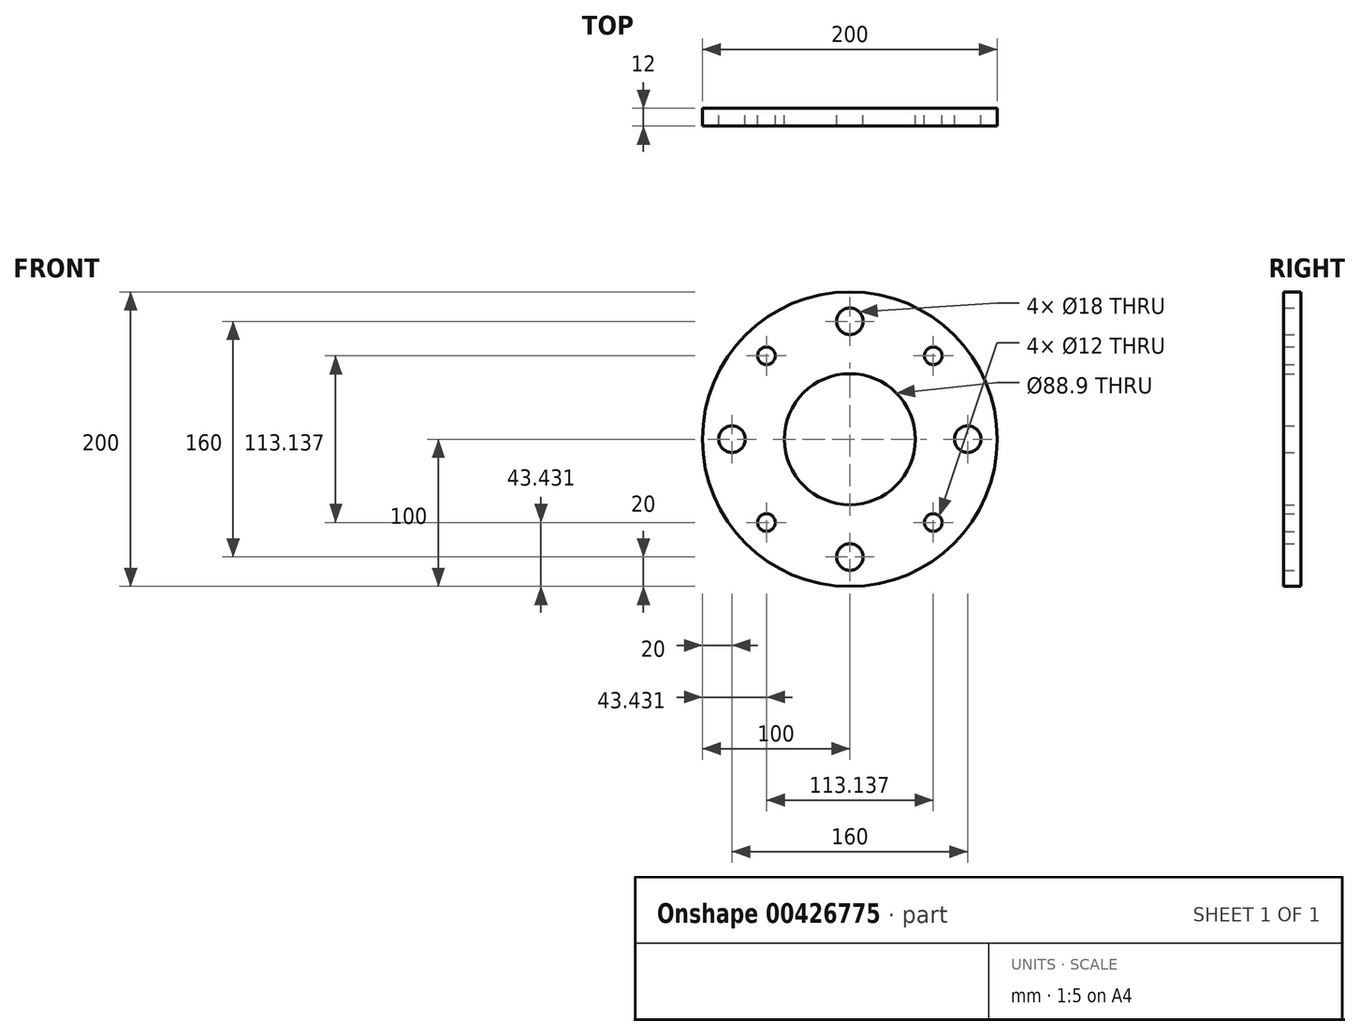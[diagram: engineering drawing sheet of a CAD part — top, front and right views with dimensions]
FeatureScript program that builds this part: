
annotation { "Feature Type Name" : "Feature", "Feature Type Description" : "" }
export const myFeature = defineFeature(function(context is Context, id is Id, definition is map)
    precondition{}
    {
        {
            var Q0;
            Q0=qCreatedBy(makeId("Front.planeOp"),FACE);
            var sketch = newSketch(context, id + "F0", { "sketchPlane" : qUnion([Q0])});
            skCircle(sketch, "E0", {"center": v(0, 0) * mm, "radius": 44.45 * mm});
            skCircle(sketch, "E1", {"center": v(0, 0) * mm, "radius": 100 * mm});
            skCircle(sketch, "E2", {"center": v(0, 0) * mm, "radius": 80 * mm, "construction": true});
            skCircle(sketch, "E3", {"center": v(0, 80) * mm, "radius": 9 * mm});
            skLineSegment(sketch, "E4", {"start": v(0, 0) * mm, "end": v(56.57, 56.57) * mm, "construction": true});
            skCircle(sketch, "E5", {"center": v(56.57, 56.57) * mm, "radius": 6 * mm});
            skCircle(sketch, "E6.1.0", {"center": v(-56.57, 56.57) * mm, "radius": 6 * mm});
            skCircle(sketch, "E7.1.0", {"center": v(-80, 0) * mm, "radius": 9 * mm});
            skCircle(sketch, "E7.2.0", {"center": v(0, -80) * mm, "radius": 9 * mm});
            skCircle(sketch, "E8.1.3.0", {"center": v(80, 0) * mm, "radius": 9 * mm});
            skCircle(sketch, "E9.1.2.0", {"center": v(-56.57, -56.57) * mm, "radius": 6 * mm});
            skCircle(sketch, "E9.1.3.0", {"center": v(56.57, -56.57) * mm, "radius": 6 * mm});
            skSolve(sketch);
        }
        {
            var Q0;
            Q0=makeQuery(id+"F0.imprint","IMPRINT",FACE,{"disambiguationData":[TD([[makeQuery(id+"F0.imprint","IMPRINT",EDGE,{"derivedFrom":sQuery(id+"F0.wireOp",EDGE,"E0")}),-1.0]])]});
            extrude(context, id + "F1", {"entities" : qUnion([Q0]), "depth" : 12 * mm});
        }
    });
